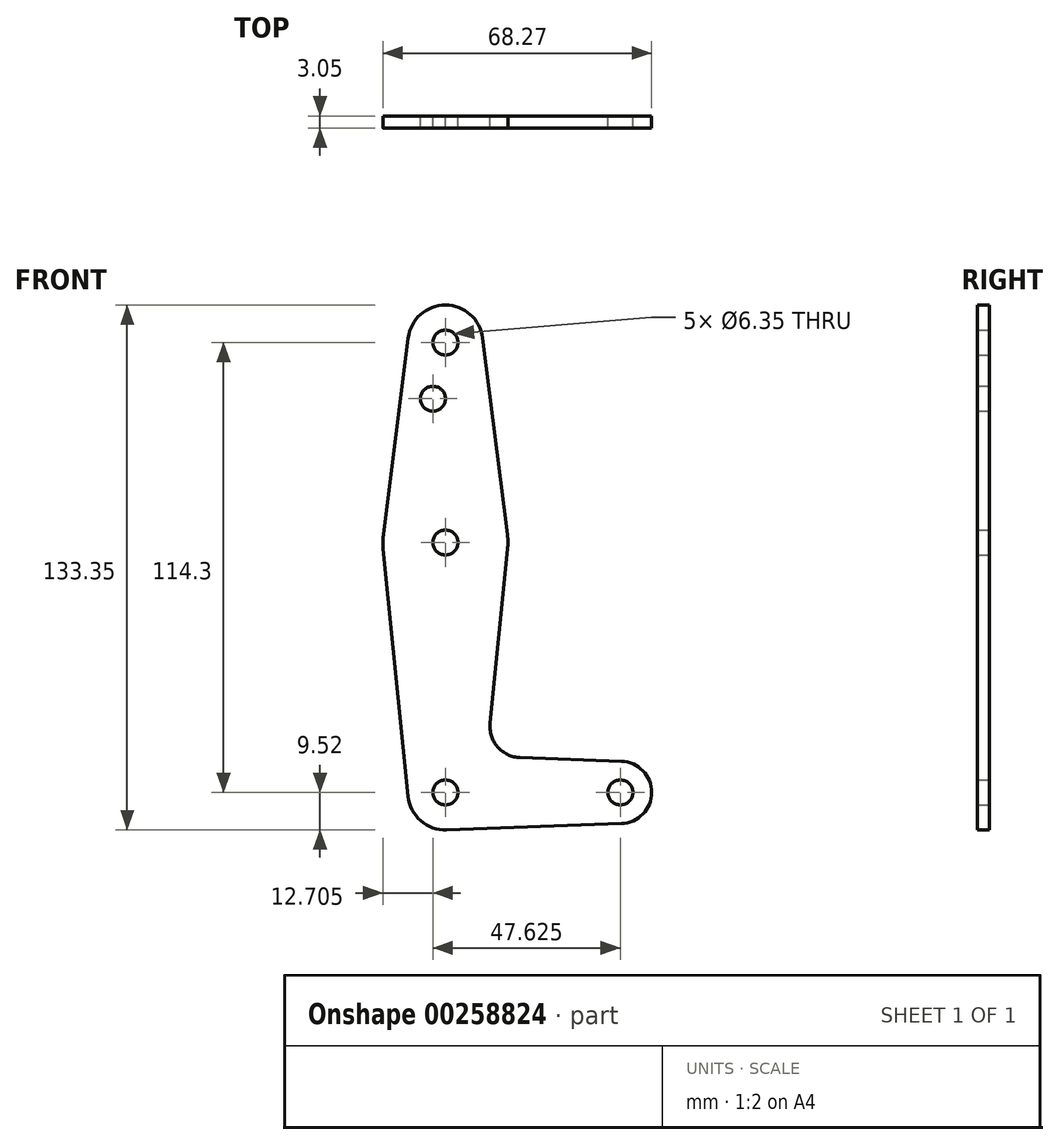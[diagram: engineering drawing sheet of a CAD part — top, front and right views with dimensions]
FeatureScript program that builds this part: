
annotation { "Feature Type Name" : "Feature", "Feature Type Description" : "" }
export const myFeature = defineFeature(function(context is Context, id is Id, definition is map)
    precondition{}
    {
        {
            var Q0;
            Q0=qCreatedBy(makeId("Front.planeOp"),FACE);
            var sketch = newSketch(context, id + "F0", { "sketchPlane" : qUnion([Q0])});
            skLineSegment(sketch, "E0", {"start": v(0, 114.3) * mm, "end": v(0, 0) * mm, "construction": true});
            skLineSegment(sketch, "E1", {"start": v(0, 0) * mm, "end": v(44.45, 0) * mm, "construction": true});
            skCircle(sketch, "E2", {"center": v(0, 114.3) * mm, "radius": 9.53 * mm});
            skCircle(sketch, "E3", {"center": v(0, 63.5) * mm, "radius": 15.88 * mm});
            skCircle(sketch, "E4", {"center": v(0, 0) * mm, "radius": 9.53 * mm});
            skCircle(sketch, "E5", {"center": v(44.45, 0) * mm, "radius": 7.94 * mm});
            skLineSegment(sketch, "E6", {"start": v(-15.75, 65.48) * mm, "end": v(-9.45, 115.5) * mm});
            skLineSegment(sketch, "E7", {"start": v(9.45, 115.5) * mm, "end": v(15.75, 65.48) * mm});
            skCircle(sketch, "E8", {"center": v(0, 114.3) * mm, "radius": 3.18 * mm});
            skCircle(sketch, "E9", {"center": v(-3.17, 100.03) * mm, "radius": 3.18 * mm});
            skCircle(sketch, "E10", {"center": v(0, 63.5) * mm, "radius": 3.18 * mm});
            skCircle(sketch, "E11", {"center": v(0, 0) * mm, "radius": 3.18 * mm});
            skCircle(sketch, "E12", {"center": v(44.45, 0) * mm, "radius": 3.18 * mm});
            skLineSegment(sketch, "E13", {"start": v(-15.8, 61.91) * mm, "end": v(-9.48, -0.95) * mm});
            skLineSegment(sketch, "E14", {"start": v(15.8, 61.91) * mm, "end": v(11.34, 17.6) * mm});
            skLineSegment(sketch, "E15", {"start": v(0.34, -9.52) * mm, "end": v(44.73, -7.93) * mm});
            skLineSegment(sketch, "E16", {"start": v(18.97, 8.85) * mm, "end": v(44.73, 7.93) * mm});
            skArc(sketch, "E17.filletArc", {"start": v(11.34, 17.6) * mm, "mid": v(13.26, 11.57) * mm, "end": v(18.97, 8.85) * mm});
            skSolve(sketch);
        }
        {
            var Q0;
            Q0 = qSketchRegion(id + "F0", true);
            extrude(context, id + "F1", {"entities" : qUnion([Q0]), "depth" : 3.05 * mm});
        }
    });
